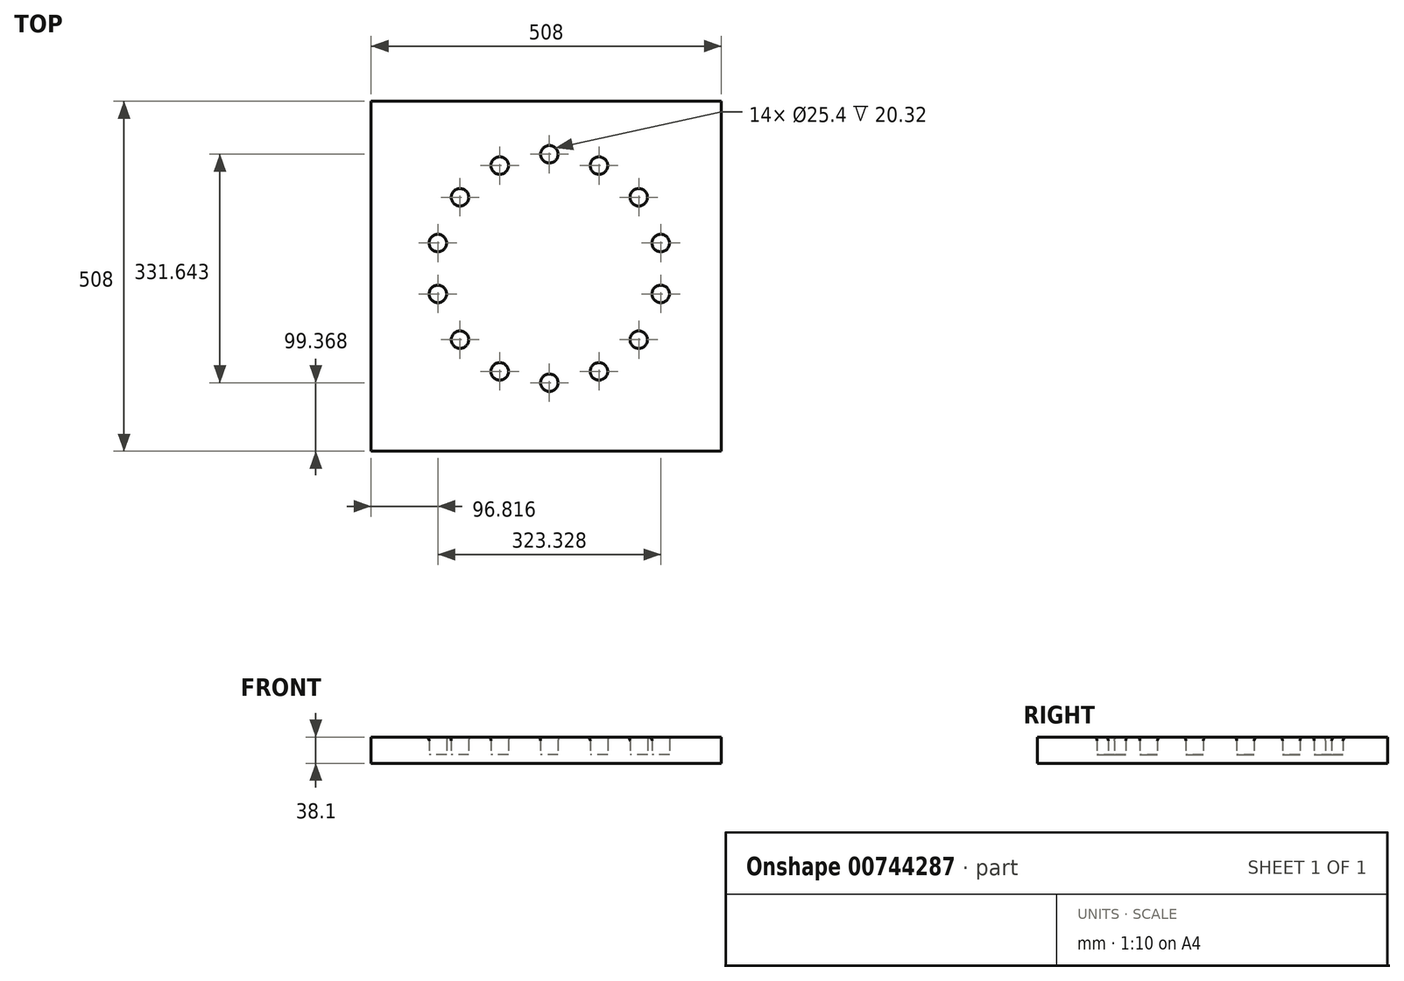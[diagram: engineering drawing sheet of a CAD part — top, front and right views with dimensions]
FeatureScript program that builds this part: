
annotation { "Feature Type Name" : "Feature", "Feature Type Description" : "" }
export const myFeature = defineFeature(function(context is Context, id is Id, definition is map)
    precondition{}
    {
        {
            var Q0;
            Q0=qCreatedBy(makeId("Top.planeOp"),FACE);
            var sketch = newSketch(context, id + "F0", { "sketchPlane" : qUnion([Q0])});
            skLineSegment(sketch, "E0.bottom", {"start": v(-258.48, 242.8) * mm, "end": v(249.52, 242.8) * mm});
            skLineSegment(sketch, "E0.top", {"start": v(-258.48, -265.2) * mm, "end": v(249.52, -265.2) * mm});
            skLineSegment(sketch, "E0.left", {"start": v(-258.48, 242.8) * mm, "end": v(-258.48, -265.2) * mm});
            skLineSegment(sketch, "E0.right", {"start": v(249.52, 242.8) * mm, "end": v(249.52, -265.2) * mm});
            skCircle(sketch, "E1", {"center": v(0, 165.82) * mm, "radius": 12.7 * mm});
            skCircle(sketch, "E2.1.0", {"center": v(71.95, 149.4) * mm, "radius": 12.7 * mm});
            skCircle(sketch, "E2.2.0", {"center": v(129.64, 103.39) * mm, "radius": 12.7 * mm});
            skCircle(sketch, "E2.3.0", {"center": v(161.66, 36.9) * mm, "radius": 12.7 * mm});
            skCircle(sketch, "E2.4.0", {"center": v(161.66, -36.9) * mm, "radius": 12.7 * mm});
            skCircle(sketch, "E2.5.0", {"center": v(129.64, -103.39) * mm, "radius": 12.7 * mm});
            skCircle(sketch, "E2.6.0", {"center": v(71.95, -149.4) * mm, "radius": 12.7 * mm});
            skCircle(sketch, "E2.7.0", {"center": v(0, -165.82) * mm, "radius": 12.7 * mm});
            skCircle(sketch, "E2.8.0", {"center": v(-71.95, -149.4) * mm, "radius": 12.7 * mm});
            skCircle(sketch, "E2.9.0", {"center": v(-129.64, -103.39) * mm, "radius": 12.7 * mm});
            skCircle(sketch, "E2.10.0", {"center": v(-161.66, -36.9) * mm, "radius": 12.7 * mm});
            skCircle(sketch, "E2.11.0", {"center": v(-161.66, 36.9) * mm, "radius": 12.7 * mm});
            skCircle(sketch, "E2.12.0", {"center": v(-129.64, 103.39) * mm, "radius": 12.7 * mm});
            skCircle(sketch, "E2.13.0", {"center": v(-71.95, 149.4) * mm, "radius": 12.7 * mm});
            skPoint(sketch, "E2.center", {"position": v(0, 0) * mm});
            skLineSegment(sketch, "E2.anchor1", {"start": v(0, 0) * mm, "end": v(0, 165.82) * mm, "construction": true});
            skLineSegment(sketch, "E2.anchor2", {"start": v(0, 0) * mm, "end": v(-71.95, 149.4) * mm, "construction": true});
            skSolve(sketch);
        }
        {
            var Q0;
            Q0=makeQuery(id+"F0.imprint","IMPRINT",FACE,{"disambiguationData":[TD([[makeQuery(id+"F0.imprint","IMPRINT",EDGE,{"derivedFrom":sQuery(id+"F0.wireOp",EDGE,"E0.bottom")}),-1.0]])]});
            extrude(context, id + "F1", {"entities" : qUnion([Q0]), "depth" : 25.4 * mm, "offsetDistance" : 25.4 * mm});
        }
        {
            var Q0;
            Q0=makeQuery(id+"F1.opExtrude","CAP_EDGE",EDGE,{"disambiguationData":[OSD([sQuery(id+"F0.wireOp",EDGE,"E1")])],"isStart":false});
            var Q1;
            Q1=makeQuery(id+"F1.opExtrude","CAP_EDGE",EDGE,{"disambiguationData":[OSD([sQuery(id+"F0.wireOp",EDGE,"E2.2.0")])],"isStart":false});
            var Q2;
            Q2=makeQuery(id+"F1.opExtrude","CAP_EDGE",EDGE,{"disambiguationData":[OSD([sQuery(id+"F0.wireOp",EDGE,"E2.1.0")])],"isStart":false});
            var Q3;
            Q3=makeQuery(id+"F1.opExtrude","CAP_EDGE",EDGE,{"disambiguationData":[OSD([sQuery(id+"F0.wireOp",EDGE,"E2.3.0")])],"isStart":false});
            var Q4;
            Q4=makeQuery(id+"F1.opExtrude","CAP_EDGE",EDGE,{"disambiguationData":[OSD([sQuery(id+"F0.wireOp",EDGE,"E2.4.0")])],"isStart":false});
            var Q5;
            Q5=makeQuery(id+"F1.opExtrude","CAP_EDGE",EDGE,{"disambiguationData":[OSD([sQuery(id+"F0.wireOp",EDGE,"E2.5.0")])],"isStart":false});
            var Q6;
            Q6=makeQuery(id+"F1.opExtrude","CAP_EDGE",EDGE,{"disambiguationData":[OSD([sQuery(id+"F0.wireOp",EDGE,"E2.6.0")])],"isStart":false});
            var Q7;
            Q7=makeQuery(id+"F1.opExtrude","CAP_EDGE",EDGE,{"disambiguationData":[OSD([sQuery(id+"F0.wireOp",EDGE,"E2.7.0")])],"isStart":false});
            var Q8;
            Q8=makeQuery(id+"F1.opExtrude","CAP_EDGE",EDGE,{"disambiguationData":[OSD([sQuery(id+"F0.wireOp",EDGE,"E2.8.0")])],"isStart":false});
            var Q9;
            Q9=makeQuery(id+"F1.opExtrude","CAP_EDGE",EDGE,{"disambiguationData":[OSD([sQuery(id+"F0.wireOp",EDGE,"E2.9.0")])],"isStart":false});
            var Q10;
            Q10=makeQuery(id+"F1.opExtrude","CAP_EDGE",EDGE,{"disambiguationData":[OSD([sQuery(id+"F0.wireOp",EDGE,"E2.10.0")])],"isStart":false});
            var Q11;
            Q11=makeQuery(id+"F1.opExtrude","CAP_EDGE",EDGE,{"disambiguationData":[OSD([sQuery(id+"F0.wireOp",EDGE,"E2.11.0")])],"isStart":false});
            var Q12;
            Q12=makeQuery(id+"F1.opExtrude","CAP_EDGE",EDGE,{"disambiguationData":[OSD([sQuery(id+"F0.wireOp",EDGE,"E2.12.0")])],"isStart":false});
            var Q13;
            Q13=makeQuery(id+"F1.opExtrude","CAP_EDGE",EDGE,{"disambiguationData":[OSD([sQuery(id+"F0.wireOp",EDGE,"E2.13.0")])],"isStart":false});
            fillet(context, id + "F2", {"entities" : qUnion([Q0, Q1, Q2, Q3, Q4, Q5, Q6, Q7, Q8, Q9, Q10, Q11, Q12, Q13]), "radius" : 5.08 * mm, "tangentPropagation" : true, "allowEdgeOverflow" : false});
        }
        {
            var Q0;
            Q0=makeQuery(id+"F1.opExtrude","CAP_FACE",FACE,{"disambiguationData":[OSD([sQuery(id+"F0.wireOp",EDGE,"E0.bottom"),sQuery(id+"F0.wireOp",EDGE,"E0.top"),sQuery(id+"F0.wireOp",EDGE,"E0.left"),sQuery(id+"F0.wireOp",EDGE,"E0.right"),sQuery(id+"F0.wireOp",EDGE,"E1"),sQuery(id+"F0.wireOp",EDGE,"E2.1.0"),sQuery(id+"F0.wireOp",EDGE,"E2.2.0"),sQuery(id+"F0.wireOp",EDGE,"E2.3.0"),sQuery(id+"F0.wireOp",EDGE,"E2.4.0"),sQuery(id+"F0.wireOp",EDGE,"E2.5.0"),sQuery(id+"F0.wireOp",EDGE,"E2.6.0"),sQuery(id+"F0.wireOp",EDGE,"E2.7.0"),sQuery(id+"F0.wireOp",EDGE,"E2.8.0"),sQuery(id+"F0.wireOp",EDGE,"E2.9.0"),sQuery(id+"F0.wireOp",EDGE,"E2.10.0"),sQuery(id+"F0.wireOp",EDGE,"E2.11.0"),sQuery(id+"F0.wireOp",EDGE,"E2.12.0"),sQuery(id+"F0.wireOp",EDGE,"E2.13.0")])],"isStart":true});
            cPlane(context, id + "F3", {"entities" : qUnion([Q0]), "cplaneType" : CPlaneType.OFFSET, "offset" : 0 * mm, "oppositeDirection" : true, "width" : 152.4 * mm, "height" : 152.4 * mm});
        }
        {
            var Q0;
            Q0=qCreatedBy(id+"F3.planeOp",FACE);
            var sketch = newSketch(context, id + "F4", { "sketchPlane" : qUnion([Q0])});
            skLineSegment(sketch, "E3.bottom", {"start": v(249.52, 265.2) * mm, "end": v(-258.48, 265.2) * mm});
            skLineSegment(sketch, "E3.top", {"start": v(249.52, -242.8) * mm, "end": v(-258.48, -242.8) * mm});
            skLineSegment(sketch, "E3.left", {"start": v(249.52, 265.2) * mm, "end": v(249.52, -242.8) * mm});
            skLineSegment(sketch, "E3.right", {"start": v(-258.48, 265.2) * mm, "end": v(-258.48, -242.8) * mm});
            skLineSegment(sketch, "E4.bottom", {"start": v(-258.48, -242.8) * mm, "end": v(-258.48, -242.8) * mm});
            skLineSegment(sketch, "E4.top", {"start": v(-258.48, -242.8) * mm, "end": v(-258.48, -242.8) * mm});
            skLineSegment(sketch, "E4.left", {"start": v(-258.48, -242.8) * mm, "end": v(-258.48, -242.8) * mm});
            skLineSegment(sketch, "E4.right", {"start": v(-258.48, -242.8) * mm, "end": v(-258.48, -242.8) * mm});
            skPoint(sketch, "E5.0", {"position": v(-258.48, -242.8) * mm});
            skPoint(sketch, "E6.0", {"position": v(-258.48, 265.2) * mm});
            skPoint(sketch, "E7.0", {"position": v(249.52, 265.2) * mm});
            skPoint(sketch, "E8.0", {"position": v(249.52, -242.8) * mm});
            skSolve(sketch);
        }
        {
            var Q0;
            Q0=makeQuery(id+"F4.imprint","IMPRINT",FACE,{"disambiguationData":[TD([[makeQuery(id+"F4.imprint","IMPRINT",EDGE,{"derivedFrom":sQuery(id+"F4.wireOp",EDGE,"E3.bottom")}),1.0]])]});
            extrude(context, id + "F5", {"entities" : qUnion([Q0]), "operationType" : NewBodyOperationType.ADD, "depth" : 12.7 * mm, "offsetDistance" : 25.4 * mm});
        }
    });
